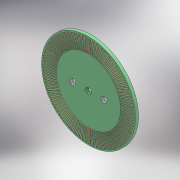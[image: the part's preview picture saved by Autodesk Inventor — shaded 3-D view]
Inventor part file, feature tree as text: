
AUTODESK INVENTOR PART (.ipt)
format: ipt  version: 2018.2 (Build 222227000, 227)  size: 875,008 bytes
history: native  units: mm
features: extrude x3, sketch x3, pattern_circular x1, plane x1, mirror x1
ambient origin geometry x8: Origin, YZ Plane, XZ Plane, XY Plane, X Axis, Y Axis, Z Axis, Center Point
bodies: Solid1 (feature_tree)
feature tree (9):
  extrude  "Extrusion1"  Depth=2.95mm
  extrude  "Extrusion2"  Depth=1.5mm
  pattern_circular  "Circular Pattern1"  [2 undecoded]
  plane  "Work Plane1"
  mirror  "Mirror1"
  extrude  "Extrusion3"  Depth=0.1mm TaperAngle=0.0deg
  sketch  "Sketch1"  dims[d0=48.0mm d1=2.95mm]
  sketch  "Sketch2"  dims[d2=1.5mm d3=0.0mm d4=0.7mm]
  sketch  "Sketch4"  dims[d5=7.0mm d6=0.75mm d7=0.1mm d8=0.0mm d9=1000.0mm d10=360.0deg d12=0.524678mm d23=8.0mm d24=8.0mm d25=3.0mm d26=3.0mm d27=10.0mm d28=0.0mm]
note: 2 required parameter values undecoded (feature->parameter linkage not recoverable at this tier; creation-order binding heuristic only, values carry confidence <= 0.55)
